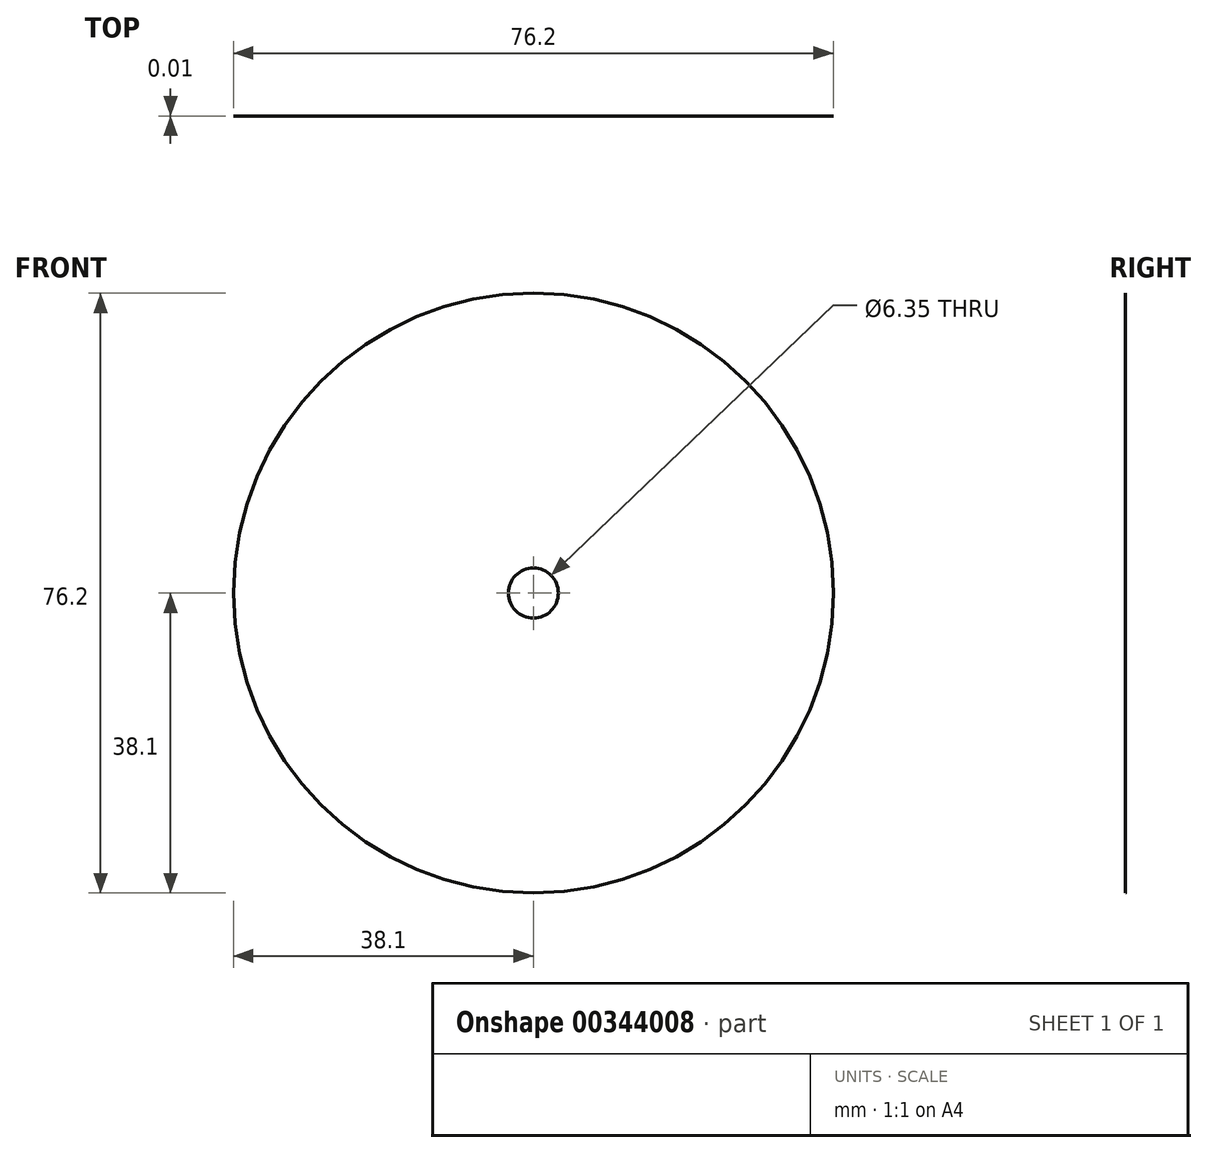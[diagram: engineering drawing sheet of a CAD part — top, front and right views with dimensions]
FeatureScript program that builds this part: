
annotation { "Feature Type Name" : "Feature", "Feature Type Description" : "" }
export const myFeature = defineFeature(function(context is Context, id is Id, definition is map)
    precondition{}
    {
        {
            var Q0;
            Q0=qCreatedBy(makeId("Front.planeOp"),FACE);
            var sketch = newSketch(context, id + "F0", { "sketchPlane" : qUnion([Q0])});
            skCircle(sketch, "E0", {"center": v(0, 0) * mm, "radius": 38.1 * mm});
            skCircle(sketch, "E1", {"center": v(0, 0) * mm, "radius": 3.18 * mm});
            skSolve(sketch);
        }
        {
            var Q0;
            Q0 = qSketchRegion(id + "F0", true);
            extrude(context, id + "F1", {"entities" : qUnion([Q0]), "depth" : 3 / 406.4 * mm});
        }
    });
